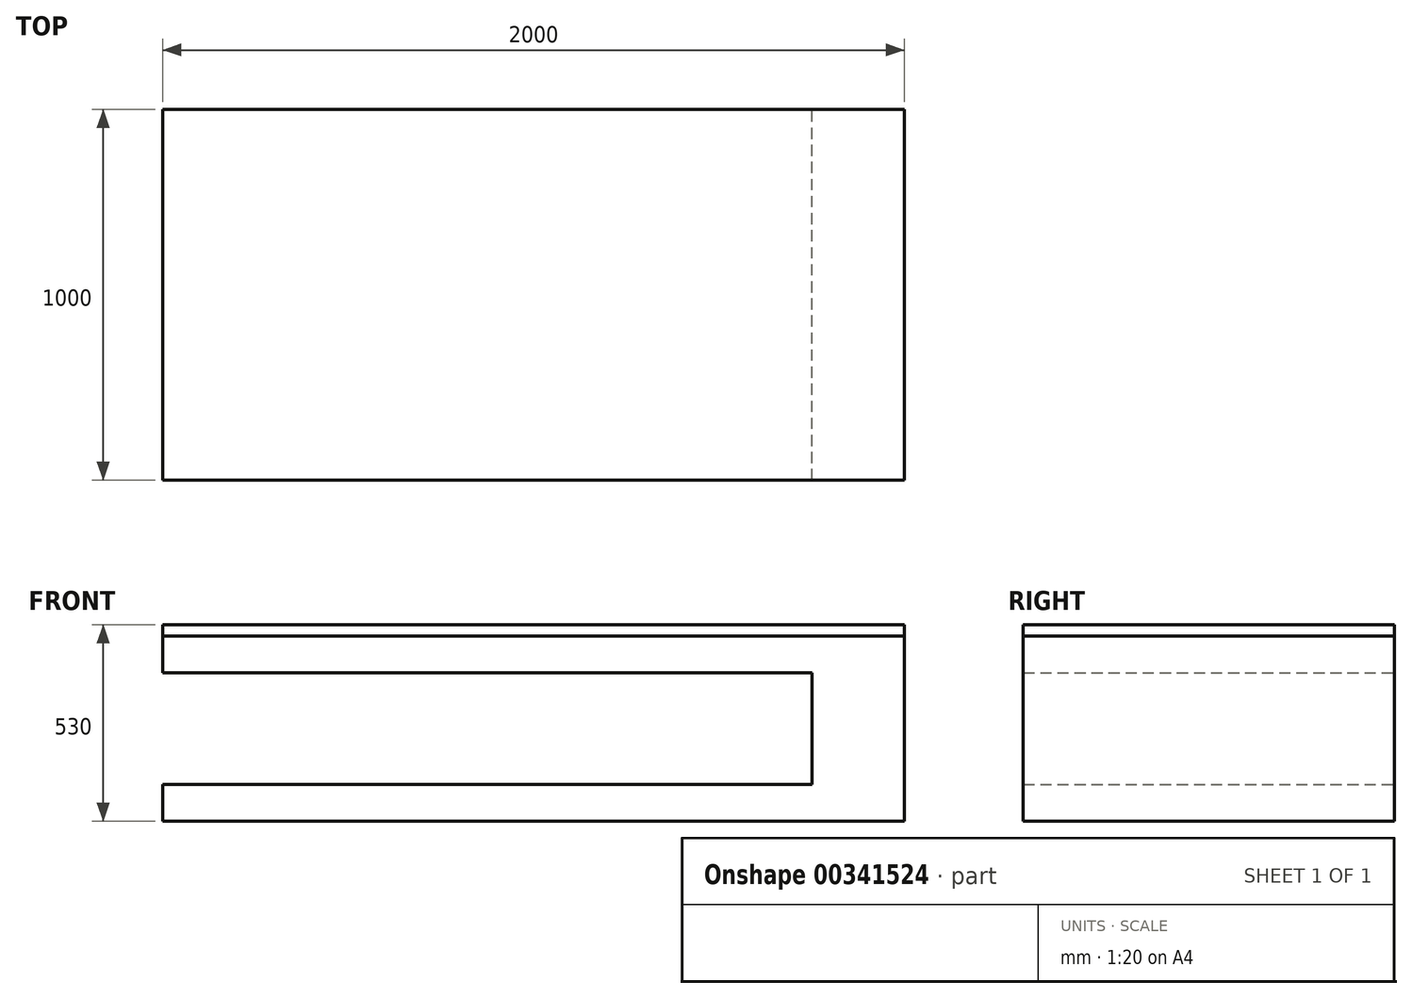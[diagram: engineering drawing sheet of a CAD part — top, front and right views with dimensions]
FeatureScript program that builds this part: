
annotation { "Feature Type Name" : "Feature", "Feature Type Description" : "" }
export const myFeature = defineFeature(function(context is Context, id is Id, definition is map)
    precondition{}
    {
        {
            var Q0;
            Q0=qCreatedBy(makeId("Front.planeOp"),FACE);
            var sketch = newSketch(context, id + "F0", { "sketchPlane" : qUnion([Q0])});
            skLineSegment(sketch, "E0.bottom", {"start": v(0, 0) * mm, "end": v(-2000, 0) * mm});
            skLineSegment(sketch, "E0.top", {"start": v(0, 500) * mm, "end": v(-2000, 500) * mm});
            skLineSegment(sketch, "E0.left", {"start": v(0, 0) * mm, "end": v(0, 500) * mm});
            skLineSegment(sketch, "E0.right", {"start": v(-2000, 0) * mm, "end": v(-2000, 500) * mm});
            skLineSegment(sketch, "E1.bottom", {"start": v(-2000, 400) * mm, "end": v(-250, 400) * mm});
            skLineSegment(sketch, "E1.top", {"start": v(-2000, 100) * mm, "end": v(-250, 100) * mm});
            skLineSegment(sketch, "E1.left", {"start": v(-2000, 400) * mm, "end": v(-2000, 100) * mm});
            skLineSegment(sketch, "E1.right", {"start": v(-250, 400) * mm, "end": v(-250, 100) * mm});
            skSolve(sketch);
        }
        {
            var Q0;
            {var subQ1=sQuery(id+"F0.wireOp",EDGE,"E0.bottom");Q0=makeQuery(id+"F0.imprint","IMPRINT",FACE,{"disambiguationData":[TD([[makeQuery(id+"F0.imprint","IMPRINT",EDGE,{"derivedFrom":subQ1}),-1.0]])]});}
            var Q1;
            Q1=qSketchRegion(id+"F2",true);
            extrude(context, id + "F1", {"entities" : qUnion([Q0, Q1]), "depth" : 1000 * mm});
        }
        {
            var Q0;
            Q0=makeQuery(id+"F1.opExtrude","CAP_FACE",FACE,{"disambiguationData":[OSD([sQuery(id+"F0.wireOp",EDGE,"E0.bottom"),sQuery(id+"F0.wireOp",EDGE,"E0.top"),sQuery(id+"F0.wireOp",EDGE,"E0.left"),sQuery(id+"F0.wireOp",EDGE,"E0.right"),sQuery(id+"F0.wireOp",EDGE,"E1.bottom"),sQuery(id+"F0.wireOp",EDGE,"E1.top"),sQuery(id+"F0.wireOp",EDGE,"E1.right")])],"isStart":false});
            var sketch = newSketch(context, id + "F2", { "sketchPlane" : qUnion([Q0])});
            skSolve(sketch);
        }
        {
            var Q0;
            {var subQ1=sQuery(id+"F0.wireOp",EDGE,"E0.bottom");Q0=makeQuery(id+"F2.imprint","IMPRINT",FACE,{"disambiguationData":[TD([[makeQuery(id+"F2.imprint","IMPRINT",EDGE,{"derivedFrom":makeQuery(id+"F1.opExtrude","CAP_EDGE",EDGE,{"disambiguationData":[OSD([subQ1])],"isStart":false})}),-1.0]])]});}
            var sketch = newSketch(context, id + "F3", { "sketchPlane" : qUnion([Q0])});
            skLineSegment(sketch, "E2.bottom", {"start": v(-2000, 500) * mm, "end": v(0, 500) * mm});
            skLineSegment(sketch, "E2.top", {"start": v(-2000, 530) * mm, "end": v(0, 530) * mm});
            skLineSegment(sketch, "E2.left", {"start": v(-2000, 500) * mm, "end": v(-2000, 530) * mm});
            skLineSegment(sketch, "E2.right", {"start": v(0, 500) * mm, "end": v(0, 530) * mm});
            skSolve(sketch);
        }
        {
            var Q0;
            Q0=makeQuery(id+"F3.imprint","IMPRINT",FACE,{"disambiguationData":[TD([[makeQuery(id+"F3.imprint","IMPRINT",EDGE,{"derivedFrom":sQuery(id+"F3.wireOp",EDGE,"E2.bottom")}),-1.0]])]});
            extrude(context, id + "F4", {"entities" : qUnion([Q0]), "oppositeDirection" : true, "depth" : 1000 * mm});
        }
    });
